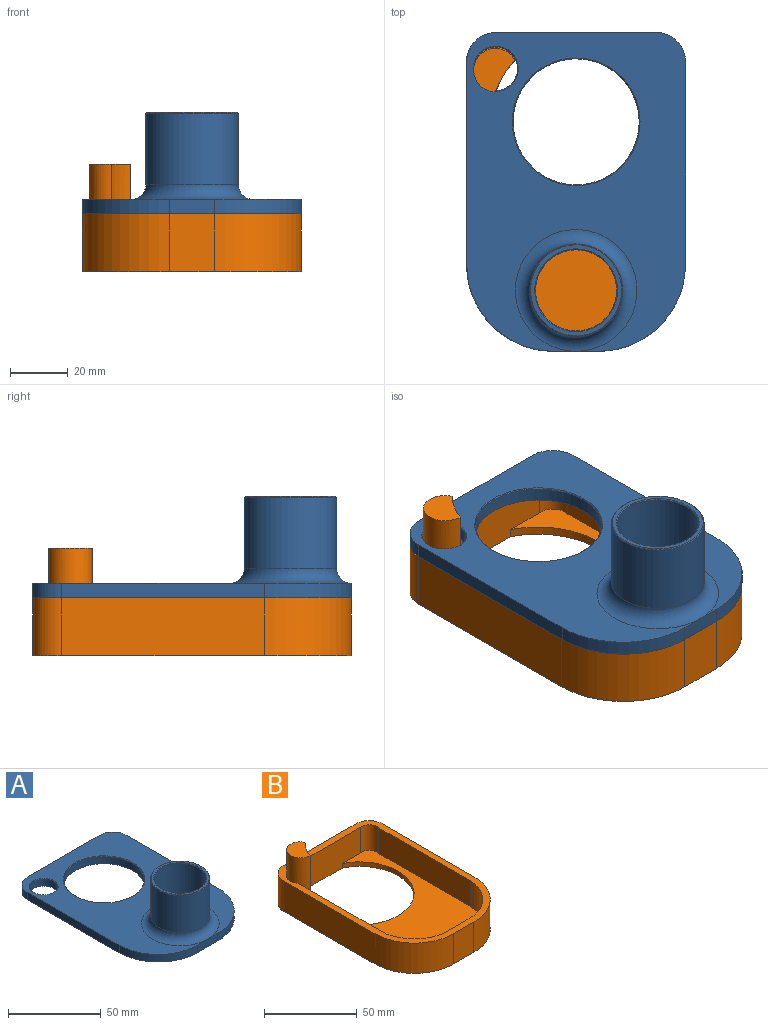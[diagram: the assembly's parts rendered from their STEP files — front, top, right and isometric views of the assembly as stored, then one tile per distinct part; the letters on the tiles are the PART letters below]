
ASSEMBLY  parts=2 mates=1
PART A: 20 faces, bbox 75.5x115.6x35 mm
  f0: plane 55.5x5mm, normal (0,1,0), area 277.5mm2, adj f1,f9,f10,f11
  f1: cylinder r=10mm len=10mm, axis (0,0,-1), area 78.5mm2, adj f0,f2,f10,f11
  f2: plane 70x5mm, normal (-1,0,0), area 350mm2, adj f1,f3,f10,f11
  f3: cylinder r=30mm len=30mm, axis (0,0,-1), area 235.6mm2, adj f2,f4,f10,f11
  f4: plane 15.5x5mm, normal (0,-1,0), area 77.5mm2, adj f3,f5,f10,f11
  f5: cylinder r=30mm len=30mm, axis (0,0,-1), area 235.6mm2, adj f4,f6,f10,f11
  f6: plane 70x5mm, normal (1,0,0), area 350mm2, adj f5,f9,f10,f11
  f7: cylinder r=21.75mm len=43.5mm, axis (0,0,-1), area 642.3mm2, adj f11,f15
  f8: cylinder r=7.5mm len=15mm, axis (0,0,-1), area 221.5mm2, adj f11,f19
  f9: cylinder r=10mm len=10mm, axis (0,0,-1), area 78.5mm2, adj f0,f6,f10,f11
  f10: plane 110x75.5mm, normal (0,0,1), area 4771.8mm2, adj f0,f1,f2,f3,f4,f5,f6,f9
  f11: plane 110x75.5mm, normal (0,0,-1), area 5597.2mm2, adj f0,f1,f2,f3,f4,f5,f6,f7
  f12: cylinder r=14mm len=34.7mm, axis (0,0,-1), area 3052.4mm2, adj f11,f17
  f13: cylinder r=16mm len=32mm, axis (0,0,-1), area 2483.1mm2, adj f16,f18
  f14: plane 31.4x31.4mm, normal (0,0,1), area 131.9mm2, adj f17,f18
  f15: cone r=21.75mm half-angle=45deg, axis (0,0,1), area 58.4mm2, adj f7,f10
  f16: torus R=21mm, axis (0,0,1), area 879.2mm2, adj f10,f13
  f17: cone r=14mm half-angle=45deg, axis (0,0,1), area 37.7mm2, adj f12,f14
  f18: cone r=15.7mm half-angle=45deg, axis (0,0,-1), area 42.3mm2, adj f13,f14
  f19: cone r=7.5mm half-angle=45deg, axis (0,0,1), area 20.4mm2, adj f8,f10
PART B: 23 faces, bbox 75.5x110x37 mm
  f0: plane 14.57x5.69mm, normal (0,0,1), area 37.8mm2, adj f8,f9,f20,f21
  f1: plane 55.5x20mm, normal (0,1,0), area 1110mm2, adj f2,f16,f17,f18
  f2: cylinder r=10mm len=20mm, axis (0,0,-1), area 314.2mm2, adj f1,f3,f17,f18
  f3: plane 70x20mm, normal (-1,0,0), area 1400mm2, adj f2,f4,f17,f18
  f4: cylinder r=30mm len=30mm, axis (0,0,-1), area 942.5mm2, adj f3,f5,f17,f18
  f5: plane 20x15.5mm, normal (0,-1,0), area 310mm2, adj f4,f6,f17,f18
  f6: cylinder r=30mm len=30mm, axis (0,0,-1), area 942.5mm2, adj f5,f7,f17,f18
  f7: plane 70x20mm, normal (1,0,0), area 1400mm2, adj f6,f16,f17,f18
  f8: plane 17x1.5mm, normal (1,0,0), area 25.5mm2, adj f0,f9,f17,f20
  f9: plane 55x20mm, normal (0,-1,0), area 1014.1mm2, adj f0,f8,f10,f17,f18,f19,f21
  f10: cylinder r=6mm len=17mm, axis (0,0,-1), area 198.7mm2, adj f9,f11,f17,f19
  f11: plane 70x17mm, normal (-1,0,0), area 1190mm2, adj f10,f12,f17,f19
  f12: cylinder r=26mm len=26.5mm, axis (0,0,-1), area 678.1mm2, adj f11,f13,f17,f19
  f13: plane 17x15.5mm, normal (0,1,0), area 263.5mm2, adj f12,f14,f17,f19
  f14: cylinder r=26mm len=25.5mm, axis (0,0,-1), area 661.1mm2, adj f13,f15,f17,f19
  f15: plane 64x17mm, normal (1,0,0), area 1088mm2, adj f14,f17,f19,f20
  f16: cylinder r=10mm len=20mm, axis (0,0,-1), area 314.2mm2, adj f1,f7,f17,f18
  f17: plane 110x75.5mm, normal (0,0,1), area 1289.8mm2, adj f1,f2,f3,f4,f5,f6,f7,f8
  f18: plane 110x75.5mm, normal (0,0,-1), area 5197mm2, adj f1,f2,f3,f4,f5,f6,f7,f9
  f19: plane 102.05x67.7mm, normal (0,0,1), area 3730.6mm2, adj f9,f10,f11,f12,f13,f14,f15,f20
  f20: cylinder r=7.5mm len=34mm, axis (0,0,-1), area 801.5mm2, adj f0,f8,f15,f17,f19,f21,f22
  f21: cylinder r=29.5mm len=59mm, axis (0,0,-1), area 911.2mm2, adj f0,f9,f18,f19,f20,f22
  f22: plane 15x14.23mm, normal (0,0,1), area 138.8mm2, adj f20,f21
PLACE A t=(8.32,50.95,16.16)mm
PLACE B t=(8.24,50.94,-3.84)mm
MATE parallel B.f17 <-> A.f11  axis (0,0,1) through (46.03,109.05,16.16)mm
